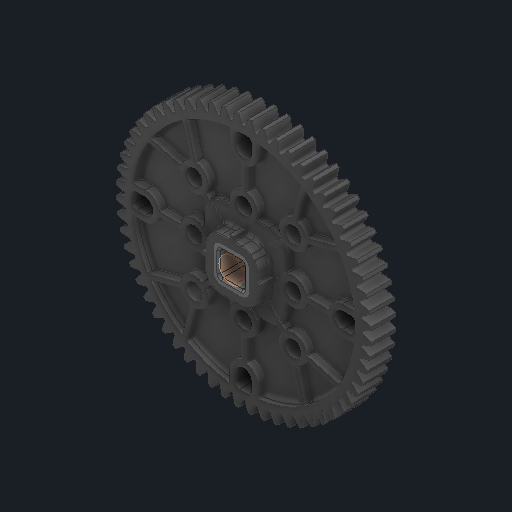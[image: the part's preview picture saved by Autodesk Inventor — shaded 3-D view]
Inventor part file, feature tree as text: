
AUTODESK INVENTOR PART (.ipt)
format: ipt  version: 2025 (Build 290162000, 162)  size: 4,851,712 bytes
history: native  units: in
note: dims shown in document units (in); Inventor stores cm internally (conversion verified against a paired STEP export)
features: other x6, sketch x3
ambient origin geometry x8: Origin, YZ Plane, XZ Plane, XY Plane, X Axis, Y Axis, Z Axis, Center Point
bodies: Solid1 (feature_tree), Solid2 (feature_tree)
feature tree (9):
  other  "Half Cut HS 60T Gear.ipt"
  other  "Solid1::Half Cut HS 60T Gear.ipt"
  other  "Solid2::Half Cut HS 60T Gear.ipt"
  other  "TaggingFeature1"
  sketch  "Sketch1"  dims[d0=0.3937in]
  sketch  "Sketch2"
  sketch  "Sketch3"
  other  "Srf1"
  other  "Srf1::Derived"
